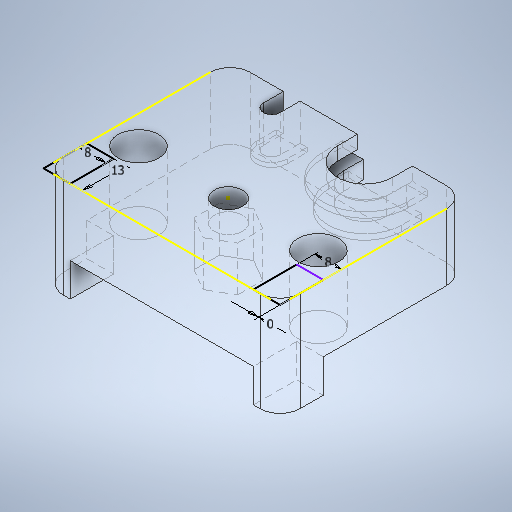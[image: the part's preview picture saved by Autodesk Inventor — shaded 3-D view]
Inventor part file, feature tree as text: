
AUTODESK INVENTOR PART (.ipt)
format: ipt  version: 2025 (Build 290162000, 162)  size: 459,264 bytes
history: native  units: mm
features: sketch x10, extrude x9, fillet x3
ambient origin geometry x8: Origin, YZ Plane, XZ Plane, XY Plane, X Axis, Y Axis, Z Axis, Center Point
bodies: Volumenkörper1 (feature_tree)
feature tree (22):
  extrude  "Extrusion1"  Depth=56.0mm
  extrude  "Extrusion2"  Depth=35.5mm
  extrude  "Extrusion3"  Depth=27.0mm
  fillet  "Rundung1"  Radius=12.25mm
  fillet  "Rundung2"  Radius=27.0mm
  sketch  "Skizze4"  dims[d8=27.0mm d9=9.0mm d10=0.0mm d11=11.0mm]
  extrude  "Extrusion5"  Depth=9.0mm TaperAngle=0.0deg
  fillet  "Rundung4"  Radius=11.0mm
  extrude  "Extrusion6"  Depth=6.0mm
  extrude  "Extrusion7"  Depth=6.0mm
  extrude  "Extrusion8"  Depth=1.67mm TaperAngle=0.0deg
  extrude  "Extrusion9"  Depth=56.0mm
  extrude  "Extrusion10"  Depth=12.25mm
  sketch  "Skizze1"  dims[d0=71.0mm d1=56.0mm]
  sketch  "Skizze2"  dims[d2=20.0mm d3=35.5mm]
  sketch  "Skizze3"  dims[d4=8.5mm d5=12.25mm d6=12.25mm d7=27.0mm]
  sketch  "Skizze5"  dims[d12=22.0mm d13=6.0mm]
  sketch  "Skizze6"  dims[d14=6.0mm d15=18.5mm]
  sketch  "Skizze7"  dims[d16=24.5mm d17=1.67mm d18=0.0mm]
  sketch  "Skizze8"  dims[d19=71.0mm d20=56.0mm]
  sketch  "Skizze9"  dims[d21=12.25mm d22=12.25mm]
  sketch  "Skizze10"  dims[d23=0.0mm d24=0.0mm d25=5.0mm d26=0.0mm d27=13.0mm d28=0.0mm d29=0.0mm d30=0.0mm d31=11.0mm d32=0.0mm d33=6.0mm d34=3.0mm d35=8.0mm d36=13.0mm d37=8.0mm d38=0.0mm d42=13.0mm d43=8.0mm d44=8.0mm d45=10.0mm d46=0.0mm d47=6.0mm d48=13.1mm d49=13.5mm d50=0.0mm d51=0.4mm d52=0.0mm d53=9.2mm d54=1.27mm d55=0.0mm d56=16.5mm d57=4.0mm d58=0.0mm d59=25.6mm d61=1.67mm d62=0.0mm]
